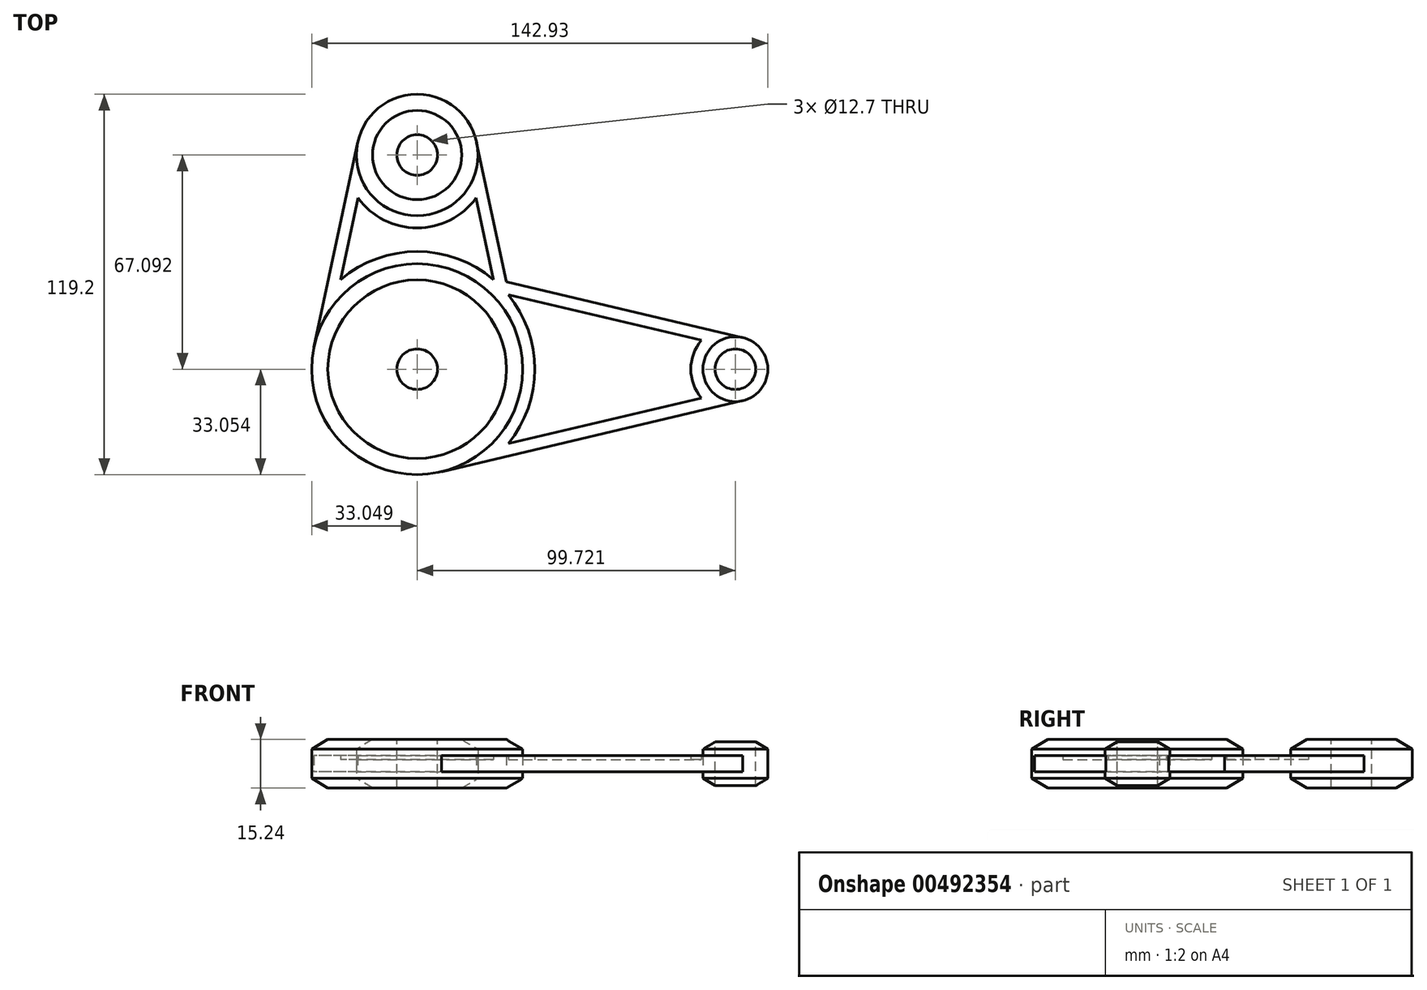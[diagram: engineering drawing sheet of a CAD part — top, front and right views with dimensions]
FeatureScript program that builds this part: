
annotation { "Feature Type Name" : "Feature", "Feature Type Description" : "" }
export const myFeature = defineFeature(function(context is Context, id is Id, definition is map)
    precondition{}
    {
        {
            var Q0;
            Q0=qCreatedBy(makeId("Top.planeOp"),FACE);
            var sketch = newSketch(context, id + "F0", { "sketchPlane" : qUnion([Q0])});
            skCircle(sketch, "E0", {"center": v(-37.52, 34.88) * mm, "radius": 19.05 * mm});
            skCircle(sketch, "E1", {"center": v(-37.52, -32.22) * mm, "radius": 33.05 * mm});
            skCircle(sketch, "E2", {"center": v(62.2, -32.22) * mm, "radius": 10.16 * mm});
            skLineSegment(sketch, "E3", {"start": v(-29.93, -0.05) * mm, "end": v(64.53, -22.33) * mm});
            skLineSegment(sketch, "E4", {"start": v(-29.93, -64.38) * mm, "end": v(64.53, -42.1) * mm});
            skLineSegment(sketch, "E5", {"start": v(-56.15, 38.85) * mm, "end": v(-69.85, -25.32) * mm});
            skLineSegment(sketch, "E6", {"start": v(-18.9, 38.85) * mm, "end": v(-5.2, -25.32) * mm});
            skLineSegment(sketch, "E7", {"start": v(48.25, -32.4) * mm, "end": v(-4.47, -32.4) * mm});
            skSolve(sketch);
        }
        {
            var Q0;
            {var subQ0=sQuery(id+"F0.wireOp",EDGE,"E1");var subQ1=makeQuery(id+"F0.imprint","INTERSECT",VERTEX,{"derivedFrom":[subQ0,sQuery(id+"F0.wireOp",EDGE,"E3")]});Q0=makeQuery(id+"F0.imprint","IMPRINT",FACE,{"disambiguationData":[TD([[makeQuery(id+"F0.imprint","IMPRINT",EDGE,{"disambiguationData":[TD([[subQ1,1.0]])],"derivedFrom":subQ0}),1.0]])]});}
            var Q1;
            {var subQ0=sQuery(id+"F0.wireOp",EDGE,"E0");var subQ1=makeQuery(id+"F0.imprint","INTERSECT",VERTEX,{"derivedFrom":[subQ0,sQuery(id+"F0.wireOp",EDGE,"E5")]});Q1=makeQuery(id+"F0.imprint","IMPRINT",FACE,{"disambiguationData":[TD([[makeQuery(id+"F0.imprint","IMPRINT",EDGE,{"disambiguationData":[TD([[subQ1,1.0]])],"derivedFrom":subQ0}),1.0]])]});}
            var Q2;
            {var subQ0=sQuery(id+"F0.wireOp",EDGE,"E2");var subQ1=makeQuery(id+"F0.imprint","INTERSECT",VERTEX,{"derivedFrom":[subQ0,sQuery(id+"F0.wireOp",EDGE,"E3")]});Q2=makeQuery(id+"F0.imprint","IMPRINT",FACE,{"disambiguationData":[TD([[makeQuery(id+"F0.imprint","IMPRINT",EDGE,{"disambiguationData":[TD([[subQ1,-1.0]])],"derivedFrom":subQ0}),1.0]])]});}
            extrude(context, id + "F1", {"entities" : qUnion([Q0, Q1, Q2]), "endBound" : BoundingType.SYMMETRIC, "depth" : 15.24 * mm});
        }
        {
            var Q0;
            Q0=makeQuery(id+"F1.opExtrude","CAP_FACE",FACE,{"disambiguationData":[OSD([sQuery(id+"F0.wireOp",EDGE,"E1")])],"isStart":false});
            var Q1;
            Q1=makeQuery(id+"F1.opExtrude","CAP_FACE",FACE,{"disambiguationData":[OSD([sQuery(id+"F0.wireOp",EDGE,"E0")])],"isStart":false});
            var Q2;
            Q2=makeQuery(id+"F1.opExtrude","CAP_FACE",FACE,{"disambiguationData":[OSD([sQuery(id+"F0.wireOp",EDGE,"E2")])],"isStart":false});
            var Q3;
            Q3=makeQuery(id+"F1.opExtrude","CAP_FACE",FACE,{"disambiguationData":[OSD([sQuery(id+"F0.wireOp",EDGE,"E1")])],"isStart":true});
            var Q4;
            Q4=makeQuery(id+"F1.opExtrude","CAP_FACE",FACE,{"disambiguationData":[OSD([sQuery(id+"F0.wireOp",EDGE,"E0")])],"isStart":true});
            var Q5;
            Q5=makeQuery(id+"F1.opExtrude","CAP_FACE",FACE,{"disambiguationData":[OSD([sQuery(id+"F0.wireOp",EDGE,"E2")])],"isStart":true});
            chamfer(context, id + "F2", {"entities" : qUnion([Q0, Q1, Q2, Q3, Q4, Q5]), "chamferType" : ChamferType.TWO_OFFSETS, "width1" : 5.08 * mm, "oppositeDirection" : false, "width2" : 3.05 * mm, "tangentPropagation" : true});
        }
        {
            var Q0;
            {var subQ5=sQuery(id+"F0.wireOp",EDGE,"E4");Q0=makeQuery(id+"F0.imprint","IMPRINT",FACE,{"disambiguationData":[TD([[makeQuery(id+"F0.imprint","IMPRINT",EDGE,{"derivedFrom":subQ5}),1.0]])]});}
            var Q1;
            {var subQ0=sQuery(id+"F0.wireOp",EDGE,"E3");var subQ1=sQuery(id+"F0.wireOp",EDGE,"E1");var subQ2=makeQuery(id+"F0.imprint","INTERSECT",VERTEX,{"derivedFrom":[subQ1,subQ0]});Q1=makeQuery(id+"F0.imprint","IMPRINT",FACE,{"disambiguationData":[TD([[makeQuery(id+"F0.imprint","IMPRINT",EDGE,{"disambiguationData":[TD([[subQ2,1.0]])],"derivedFrom":subQ1}),-1.0]])]});}
            var Q2;
            {var subQ5=sQuery(id+"F0.wireOp",EDGE,"E5");Q2=makeQuery(id+"F0.imprint","IMPRINT",FACE,{"disambiguationData":[TD([[makeQuery(id+"F0.imprint","IMPRINT",EDGE,{"derivedFrom":subQ5}),1.0]])]});}
            extrude(context, id + "F3", {"entities" : qUnion([Q0, Q1, Q2]), "endBound" : BoundingType.SYMMETRIC, "depth" : 5.08 * mm});
        }
        {
            var Q0;
            Q0=makeQuery(id+"F3.opExtrude","CAP_FACE",FACE,{"disambiguationData":[OSD([sQuery(id+"F0.wireOp",EDGE,"E0"),sQuery(id+"F0.wireOp",EDGE,"E1"),sQuery(id+"F0.wireOp",EDGE,"E2"),sQuery(id+"F0.wireOp",EDGE,"E3"),sQuery(id+"F0.wireOp",EDGE,"E4"),sQuery(id+"F0.wireOp",EDGE,"E5"),sQuery(id+"F0.wireOp",EDGE,"E6")])],"isStart":false});
            shell(context, id + "F4", {"entities" : qUnion([Q0]), "thickness" : 3.8 * mm});
        }
        {
            var Q0;
            Q0=sQuery(id+"F0.wireOp",VERTEX,"E1.center");
            var Q1;
            Q1=sQuery(id+"F0.wireOp",VERTEX,"E0.center");
            var Q2;
            Q2=sQuery(id+"F0.wireOp",VERTEX,"E2.center");
            var Q3;
            Q3=makeQuery(id+"F1.opExtrude","SWEPT_BODY",BODY,{"disambiguationData":[OSD([sQuery(id+"F0.wireOp",EDGE,"E1")])]});
            var Q4;
            Q4=makeQuery(id+"F1.opExtrude","SWEPT_BODY",BODY,{"disambiguationData":[OSD([sQuery(id+"F0.wireOp",EDGE,"E0")])]});
            var Q5;
            Q5=makeQuery(id+"F1.opExtrude","SWEPT_BODY",BODY,{"disambiguationData":[OSD([sQuery(id+"F0.wireOp",EDGE,"E2")])]});
            hole(context, id + "F5", {"style" : HoleStyle.SIMPLE, "endStyle" : HoleEndStyle.BLIND, "holeDiameter" : 12.7 * mm, "holeDepth" : 63.5 * mm, "isTappedThrough" : true, "tappedDepth" : 12.7 * mm, "tapClearance" : 3, "locations" : qUnion([Q0, Q1, Q2]), "scope" : qUnion([Q3, Q4, Q5])});
        }
        {
            var Q0;
            Q0=sQuery(id+"F0.wireOp",VERTEX,"E1.center");
            var Q1;
            Q1=sQuery(id+"F0.wireOp",VERTEX,"E0.center");
            var Q2;
            Q2=sQuery(id+"F0.wireOp",VERTEX,"E2.center");
            var Q3;
            Q3=makeQuery(id+"F1.opExtrude","SWEPT_BODY",BODY,{"disambiguationData":[OSD([sQuery(id+"F0.wireOp",EDGE,"E1")])]});
            var Q4;
            Q4=makeQuery(id+"F1.opExtrude","SWEPT_BODY",BODY,{"disambiguationData":[OSD([sQuery(id+"F0.wireOp",EDGE,"E0")])]});
            var Q5;
            Q5=makeQuery(id+"F1.opExtrude","SWEPT_BODY",BODY,{"disambiguationData":[OSD([sQuery(id+"F0.wireOp",EDGE,"E2")])]});
            hole(context, id + "F6", {"style" : HoleStyle.SIMPLE, "endStyle" : HoleEndStyle.BLIND, "oppositeDirection" : true, "holeDiameter" : 12.7 * mm, "holeDepth" : 63.5 * mm, "isTappedThrough" : true, "tappedDepth" : 12.7 * mm, "tapClearance" : 3, "startFromSketch" : true, "locations" : qUnion([Q0, Q1, Q2]), "scope" : qUnion([Q3, Q4, Q5])});
        }
    });
